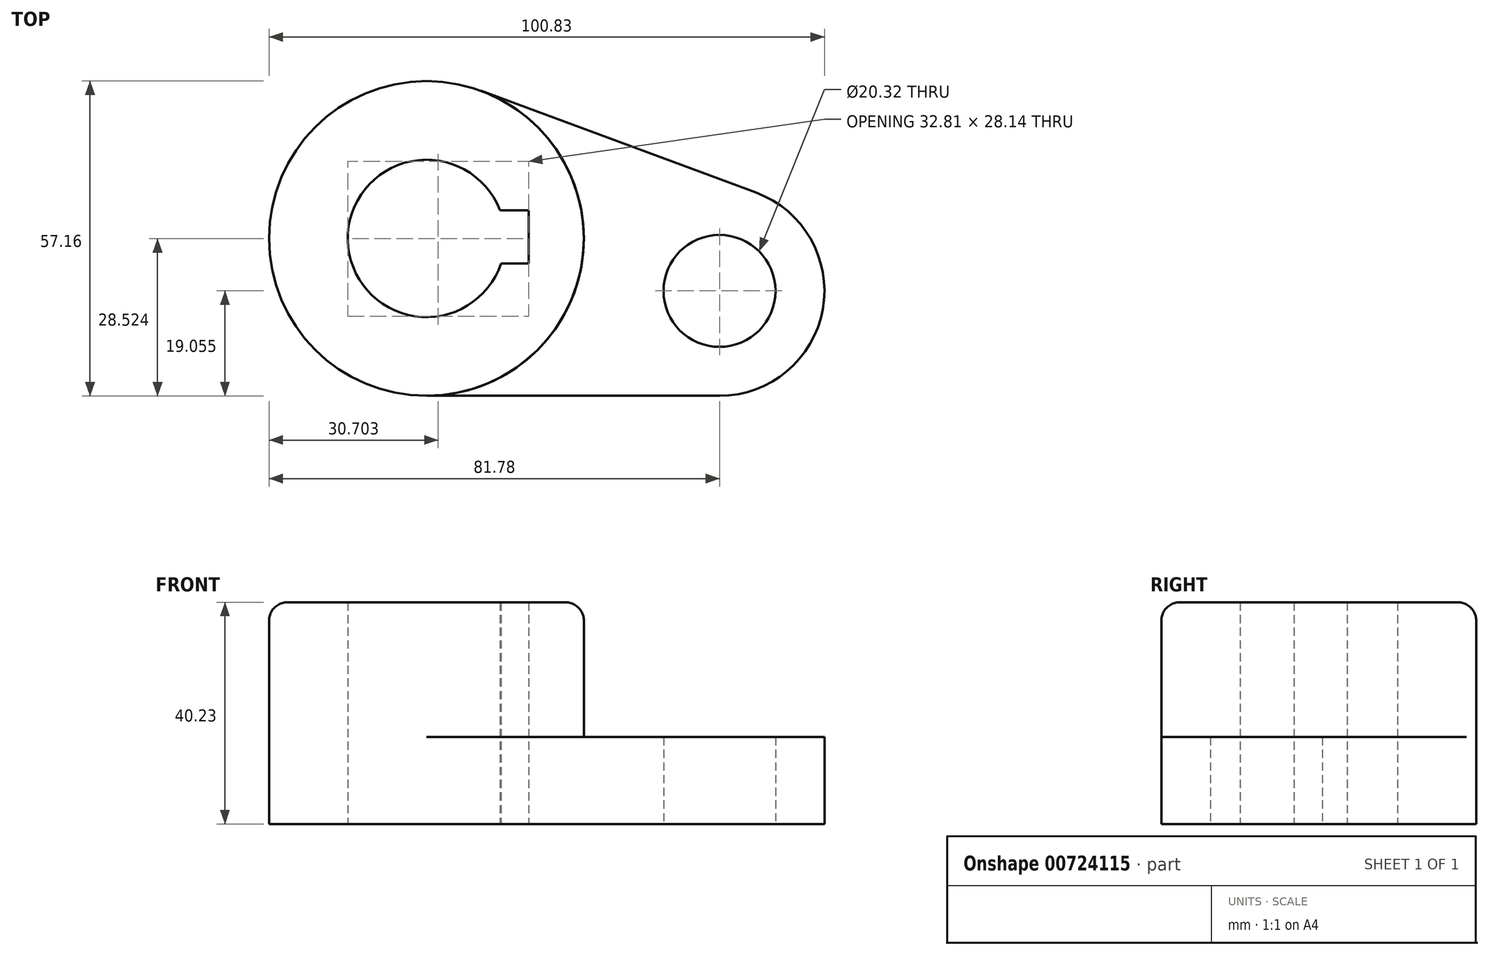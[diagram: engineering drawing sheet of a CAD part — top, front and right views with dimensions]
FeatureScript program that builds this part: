
annotation { "Feature Type Name" : "Feature", "Feature Type Description" : "" }
export const myFeature = defineFeature(function(context is Context, id is Id, definition is map)
    precondition{}
    {
        {
            var Q0;
            Q0=qCreatedBy(makeId("Top.planeOp"),FACE);
            var sketch = newSketch(context, id + "F0", { "sketchPlane" : qUnion([Q0])});
            skCircle(sketch, "E0", {"center": v(0, 0) * mm, "radius": 28.58 * mm});
            skCircle(sketch, "E1", {"center": v(53.2, -9.52) * mm, "radius": 10.16 * mm});
            skLineSegment(sketch, "E2", {"start": v(13.33, 5.13) * mm, "end": v(18.53, 5.13) * mm});
            skLineSegment(sketch, "E3", {"start": v(18.53, 5.13) * mm, "end": v(18.53, -4.52) * mm});
            skLineSegment(sketch, "E4", {"start": v(18.53, -4.52) * mm, "end": v(13.55, -4.52) * mm});
            skArc(sketch, "E5", {"start": v(13.33, 5.13) * mm, "mid": v(-14.28, -0.33) * mm, "end": v(13.55, -4.52) * mm});
            skCircle(sketch, "E6", {"center": v(53.2, -9.52) * mm, "radius": 19.05 * mm});
            skLineSegment(sketch, "E7", {"start": v(0, -28.57) * mm, "end": v(53.2, -28.57) * mm});
            skLineSegment(sketch, "E8", {"start": v(9.91, 26.8) * mm, "end": v(59.8, 8.34) * mm});
            skSolve(sketch);
        }
        {
            var Q0;
            Q0=makeQuery(id+"F0.imprint","IMPRINT",FACE,{"disambiguationData":[TD([[makeQuery(id+"F0.imprint","IMPRINT",EDGE,{"derivedFrom":sQuery(id+"F0.wireOp",EDGE,"E2")}),1.0]])]});
            extrude(context, id + "F1", {"entities" : qUnion([Q0]), "depth" : 40.23 * mm, "offsetDistance" : 25.4 * mm});
        }
        {
            var Q0;
            {var subQ0=sQuery(id+"F0.wireOp",EDGE,"E7");Q0=makeQuery(id+"F0.imprint","IMPRINT",FACE,{"disambiguationData":[TD([[makeQuery(id+"F0.imprint","IMPRINT",EDGE,{"derivedFrom":subQ0}),1.0]])]});}
            var Q1;
            Q1=makeQuery(id+"F0.imprint","IMPRINT",FACE,{"disambiguationData":[TD([[makeQuery(id+"F0.imprint","IMPRINT",EDGE,{"derivedFrom":sQuery(id+"F0.wireOp",EDGE,"E1")}),-1.0]])]});
            extrude(context, id + "F2", {"entities" : qUnion([Q0, Q1]), "operationType" : NewBodyOperationType.ADD, "depth" : 15.77 * mm, "offsetDistance" : 25.4 * mm});
        }
        {
            var Q0;
            Q0=makeQuery(id+"F1.opExtrude","CAP_EDGE",EDGE,{"disambiguationData":[OSD([sQuery(id+"F0.wireOp",EDGE,"E0")])],"isStart":false});
            fillet(context, id + "F3", {"entities" : qUnion([Q0]), "radius" : 3.3 * mm, "tangentPropagation" : true, "allowEdgeOverflow" : false});
        }
    });
